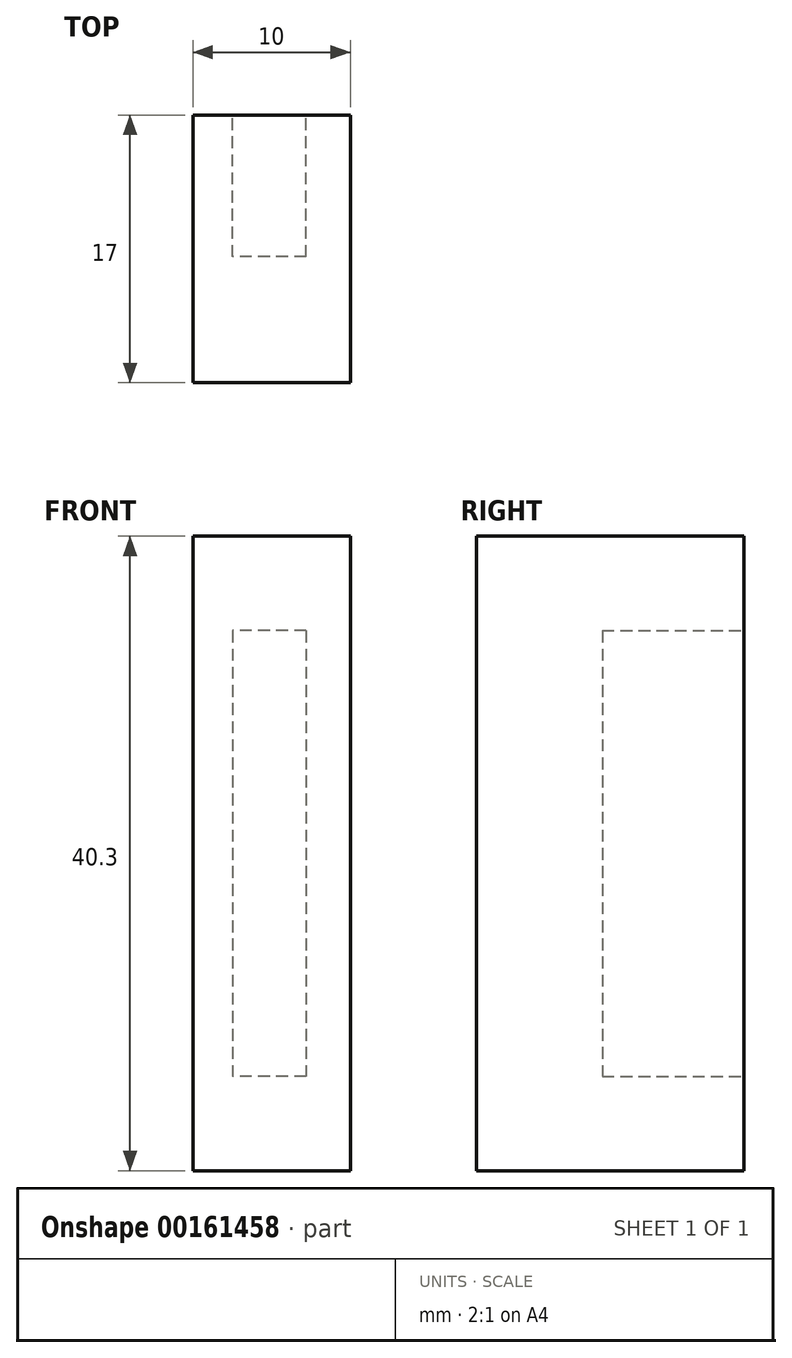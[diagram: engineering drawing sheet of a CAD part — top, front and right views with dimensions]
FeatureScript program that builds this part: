
annotation { "Feature Type Name" : "Feature", "Feature Type Description" : "" }
export const myFeature = defineFeature(function(context is Context, id is Id, definition is map)
    precondition{}
    {
        {
            var Q0;
            Q0=qCreatedBy(makeId("Front.planeOp"),FACE);
            var sketch = newSketch(context, id + "F0", { "sketchPlane" : qUnion([Q0])});
            skLineSegment(sketch, "E0.bottom", {"start": v(-30.25, -40.58) * mm, "end": v(-20.25, -40.58) * mm});
            skLineSegment(sketch, "E0.top", {"start": v(-30.25, -80.88) * mm, "end": v(-20.25, -80.88) * mm});
            skLineSegment(sketch, "E0.left", {"start": v(-30.25, -40.58) * mm, "end": v(-30.25, -80.88) * mm});
            skLineSegment(sketch, "E0.right", {"start": v(-20.25, -40.58) * mm, "end": v(-20.25, -80.88) * mm});
            skLineSegment(sketch, "E1.bottom", {"start": v(-23.06, -46.58) * mm, "end": v(-27.72, -46.58) * mm});
            skLineSegment(sketch, "E1.top", {"start": v(-23.06, -74.88) * mm, "end": v(-27.72, -74.88) * mm});
            skLineSegment(sketch, "E1.left", {"start": v(-23.06, -46.58) * mm, "end": v(-23.06, -74.88) * mm});
            skLineSegment(sketch, "E1.right", {"start": v(-27.72, -46.58) * mm, "end": v(-27.72, -74.88) * mm});
            skLineSegment(sketch, "E2", {"start": v(-23.06, -74.88) * mm, "end": v(-23.06, -80.88) * mm, "construction": true});
            skLineSegment(sketch, "E3", {"start": v(-27.72, -46.58) * mm, "end": v(-27.72, -40.58) * mm, "construction": true});
            skSolve(sketch);
        }
        {
            var Q0;
            Q0=makeQuery(id+"F0.imprint","IMPRINT",FACE,{"disambiguationData":[TD([[makeQuery(id+"F0.imprint","IMPRINT",EDGE,{"derivedFrom":sQuery(id+"F0.wireOp",EDGE,"E0.bottom")}),-1.0]])]});
            var Q1;
            Q1=makeQuery(id+"F0.imprint","IMPRINT",FACE,{"disambiguationData":[TD([[makeQuery(id+"F0.imprint","IMPRINT",EDGE,{"derivedFrom":sQuery(id+"F0.wireOp",EDGE,"0H4b4fvO-dyxi-FZrW-pJNc-f5h2Ua2qFgm1.bottom")}),-1.0]])]});
            var Q2;
            Q2=makeQuery(id+"F0.imprint","IMPRINT",FACE,{"disambiguationData":[TD([[makeQuery(id+"F0.imprint","IMPRINT",EDGE,{"derivedFrom":sQuery(id+"F0.wireOp",EDGE,"RIwqPRcQ-8Yhb-SA2c-7hZh-BoyqNhFDoh6P.bottom")}),-1.0]])]});
            var Q3;
            Q3=makeQuery(id+"F0.imprint","IMPRINT",FACE,{"disambiguationData":[TD([[makeQuery(id+"F0.imprint","IMPRINT",EDGE,{"derivedFrom":sQuery(id+"F0.wireOp",EDGE,"V1CP0RN2-3pWF-4ICx-AOtc-XG8nw0NRMOAc.bottom")}),-1.0]])]});
            var Q4;
            Q4=makeQuery(id+"F0.imprint","IMPRINT",FACE,{"disambiguationData":[TD([[makeQuery(id+"F0.imprint","IMPRINT",EDGE,{"derivedFrom":sQuery(id+"F0.wireOp",EDGE,"E1.bottom")}),1.0]])]});
            extrude(context, id + "F1", {"entities" : qUnion([Q0, Q1, Q2, Q3, Q4]), "depth" : 17 * mm});
        }
        {
            var Q0;
            Q0=makeQuery(id+"F0.imprint","IMPRINT",FACE,{"disambiguationData":[TD([[makeQuery(id+"F0.imprint","IMPRINT",EDGE,{"derivedFrom":sQuery(id+"F0.wireOp",EDGE,"0H4b4fvO-dyxi-FZrW-pJNc-f5h2Ua2qFgm1.bottom")}),-1.0]])]});
            var Q1;
            Q1=makeQuery(id+"F0.imprint","IMPRINT",FACE,{"disambiguationData":[TD([[makeQuery(id+"F0.imprint","IMPRINT",EDGE,{"derivedFrom":sQuery(id+"F0.wireOp",EDGE,"RIwqPRcQ-8Yhb-SA2c-7hZh-BoyqNhFDoh6P.bottom")}),-1.0]])]});
            var Q2;
            Q2=makeQuery(id+"F0.imprint","IMPRINT",FACE,{"disambiguationData":[TD([[makeQuery(id+"F0.imprint","IMPRINT",EDGE,{"derivedFrom":sQuery(id+"F0.wireOp",EDGE,"V1CP0RN2-3pWF-4ICx-AOtc-XG8nw0NRMOAc.bottom")}),-1.0]])]});
            var Q3;
            Q3=makeQuery(id+"F0.imprint","IMPRINT",FACE,{"disambiguationData":[TD([[makeQuery(id+"F0.imprint","IMPRINT",EDGE,{"derivedFrom":sQuery(id+"F0.wireOp",EDGE,"E1.bottom")}),1.0]])]});
            extrude(context, id + "F2", {"entities" : qUnion([Q0, Q1, Q2, Q3]), "operationType" : NewBodyOperationType.REMOVE, "depth" : 9 * mm});
        }
    });
